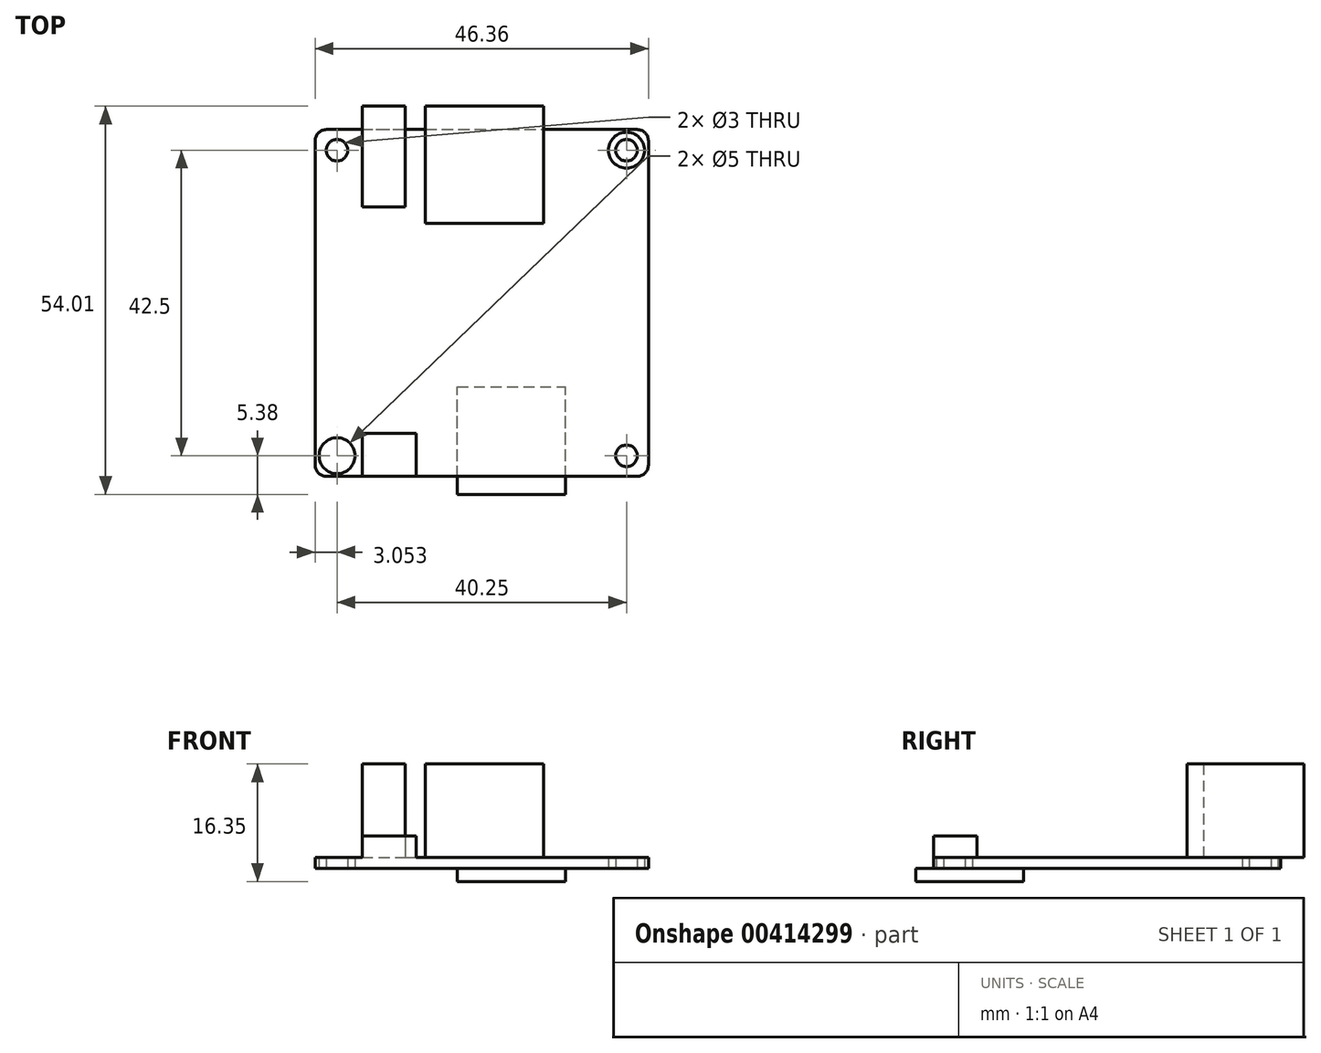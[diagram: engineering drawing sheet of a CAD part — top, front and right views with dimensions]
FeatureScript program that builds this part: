
annotation { "Feature Type Name" : "Feature", "Feature Type Description" : "" }
export const myFeature = defineFeature(function(context is Context, id is Id, definition is map)
    precondition{}
    {
        {
            var Q0;
            Q0=qCreatedBy(makeId("Top.planeOp"),FACE);
            var sketch = newSketch(context, id + "F0", { "sketchPlane" : qUnion([Q0])});
            skLineSegment(sketch, "E0.bottom", {"start": v(1.59, 0) * mm, "end": v(44.77, 0) * mm});
            skLineSegment(sketch, "E0.top", {"start": v(1.59, 48.26) * mm, "end": v(44.77, 48.26) * mm});
            skLineSegment(sketch, "E0.left", {"start": v(0, 1.59) * mm, "end": v(0, 46.67) * mm});
            skLineSegment(sketch, "E0.right", {"start": v(46.35, 1.59) * mm, "end": v(46.35, 46.67) * mm});
            skCircle(sketch, "E1", {"center": v(43.3, 2.88) * mm, "radius": 2.5 * mm});
            skLineSegment(sketch, "E2", {"start": v(23.18, 48.26) * mm, "end": v(23.18, 0) * mm, "construction": true});
            skLineSegment(sketch, "E3", {"start": v(0, 24.13) * mm, "end": v(46.35, 24.13) * mm, "construction": true});
            skCircle(sketch, "E4", {"center": v(43.3, 2.88) * mm, "radius": 1.5 * mm});
            skCircle(sketch, "E5.MirrorC", {"center": v(43.3, 45.38) * mm, "radius": 1.5 * mm});
            skCircle(sketch, "E6.MirrorC", {"center": v(43.3, 45.38) * mm, "radius": 2.5 * mm});
            skCircle(sketch, "E7.MirrorC", {"center": v(3.05, 2.88) * mm, "radius": 2.5 * mm});
            skCircle(sketch, "E8.MirrorC", {"center": v(3.05, 45.38) * mm, "radius": 2.5 * mm});
            skCircle(sketch, "E9.MirrorC", {"center": v(3.05, 45.38) * mm, "radius": 1.5 * mm});
            skCircle(sketch, "E10.MirrorC", {"center": v(3.05, 2.88) * mm, "radius": 1.5 * mm});
            skPoint(sketch, "E11.visualSharp", {"position": v(0, 48.26) * mm});
            skArc(sketch, "E11.filletArc", {"start": v(1.59, 48.26) * mm, "mid": v(0.46, 47.8) * mm, "end": v(0, 46.67) * mm});
            skPoint(sketch, "E12.visualSharp", {"position": v(46.35, 48.26) * mm});
            skArc(sketch, "E12.filletArc", {"start": v(46.35, 46.67) * mm, "mid": v(45.9, 47.8) * mm, "end": v(44.77, 48.26) * mm});
            skPoint(sketch, "E13.visualSharp", {"position": v(0, 0) * mm});
            skArc(sketch, "E13.filletArc", {"start": v(0, 1.59) * mm, "mid": v(0.46, 0.46) * mm, "end": v(1.59, 0) * mm});
            skPoint(sketch, "E14.visualSharp", {"position": v(46.35, 0) * mm});
            skArc(sketch, "E14.filletArc", {"start": v(44.77, 0) * mm, "mid": v(45.9, 0.46) * mm, "end": v(46.35, 1.59) * mm});
            skSolve(sketch);
        }
        {
            var Q0;
            Q0=makeQuery(id+"F0.imprint","IMPRINT",FACE,{"disambiguationData":[TD([[makeQuery(id+"F0.imprint","IMPRINT",EDGE,{"derivedFrom":sQuery(id+"F0.wireOp",EDGE,"E0.bottom")}),1.0]])]});
            var Q1;
            Q1=makeQuery(id+"F0.imprint","IMPRINT",FACE,{"disambiguationData":[TD([[makeQuery(id+"F0.imprint","IMPRINT",EDGE,{"derivedFrom":sQuery(id+"F0.wireOp",EDGE,"E7.MirrorC")}),-1.0]])]});
            var Q2;
            Q2=makeQuery(id+"F0.imprint","IMPRINT",FACE,{"disambiguationData":[TD([[makeQuery(id+"F0.imprint","IMPRINT",EDGE,{"derivedFrom":sQuery(id+"F0.wireOp",EDGE,"E1")}),1.0]])]});
            var Q3;
            Q3=makeQuery(id+"F0.imprint","IMPRINT",FACE,{"disambiguationData":[TD([[makeQuery(id+"F0.imprint","IMPRINT",EDGE,{"derivedFrom":sQuery(id+"F0.wireOp",EDGE,"E5.MirrorC")}),1.0]])]});
            var Q4;
            Q4=makeQuery(id+"F0.imprint","IMPRINT",FACE,{"disambiguationData":[TD([[makeQuery(id+"F0.imprint","IMPRINT",EDGE,{"derivedFrom":sQuery(id+"F0.wireOp",EDGE,"E8.MirrorC")}),1.0]])]});
            extrude(context, id + "F1", {"entities" : qUnion([Q0, Q1, Q2, Q3, Q4]), "depth" : 1.5 * mm});
        }
        {
            var Q0;
            Q0=makeQuery(id+"F1.opExtrude","CAP_FACE",FACE,{"disambiguationData":[OSD([sQuery(id+"F0.wireOp",EDGE,"E0.bottom"),sQuery(id+"F0.wireOp",EDGE,"E0.top"),sQuery(id+"F0.wireOp",EDGE,"E0.left"),sQuery(id+"F0.wireOp",EDGE,"E0.right"),sQuery(id+"F0.wireOp",EDGE,"E4"),sQuery(id+"F0.wireOp",EDGE,"E5.MirrorC"),sQuery(id+"F0.wireOp",EDGE,"E9.MirrorC"),sQuery(id+"F0.wireOp",EDGE,"E10.MirrorC"),sQuery(id+"F0.wireOp",EDGE,"E11.filletArc"),sQuery(id+"F0.wireOp",EDGE,"E12.filletArc"),sQuery(id+"F0.wireOp",EDGE,"E13.filletArc"),sQuery(id+"F0.wireOp",EDGE,"E14.filletArc")])],"isStart":false});
            var sketch = newSketch(context, id + "F2", { "sketchPlane" : qUnion([Q0])});
            skLineSegment(sketch, "E15.bottom", {"start": v(6.55, 51.51) * mm, "end": v(12.55, 51.51) * mm});
            skLineSegment(sketch, "E15.top", {"start": v(6.55, 37.51) * mm, "end": v(12.55, 37.51) * mm});
            skLineSegment(sketch, "E15.left", {"start": v(6.55, 51.51) * mm, "end": v(6.55, 37.51) * mm});
            skLineSegment(sketch, "E15.right", {"start": v(12.55, 51.51) * mm, "end": v(12.55, 37.51) * mm});
            skLineSegment(sketch, "E16.bottom", {"start": v(15.3, 51.51) * mm, "end": v(31.8, 51.51) * mm});
            skLineSegment(sketch, "E16.top", {"start": v(15.3, 35.21) * mm, "end": v(31.8, 35.21) * mm});
            skLineSegment(sketch, "E16.left", {"start": v(15.3, 51.51) * mm, "end": v(15.3, 35.21) * mm});
            skLineSegment(sketch, "E16.right", {"start": v(31.8, 51.51) * mm, "end": v(31.8, 35.21) * mm});
            skLineSegment(sketch, "E17.bottom", {"start": v(6.55, 0) * mm, "end": v(14.05, 0) * mm});
            skLineSegment(sketch, "E17.top", {"start": v(6.55, 6) * mm, "end": v(14.05, 6) * mm});
            skLineSegment(sketch, "E17.left", {"start": v(6.55, 0) * mm, "end": v(6.55, 6) * mm});
            skLineSegment(sketch, "E17.right", {"start": v(14.05, 0) * mm, "end": v(14.05, 6) * mm});
            skLineSegment(sketch, "E18.bottom", {"start": v(19.8, -2.5) * mm, "end": v(34.8, -2.5) * mm});
            skLineSegment(sketch, "E18.top", {"start": v(19.8, 12.5) * mm, "end": v(34.8, 12.5) * mm});
            skLineSegment(sketch, "E18.left", {"start": v(19.8, -2.5) * mm, "end": v(19.8, 12.5) * mm});
            skLineSegment(sketch, "E18.right", {"start": v(34.8, -2.5) * mm, "end": v(34.8, 12.5) * mm});
            skSolve(sketch);
        }
        {
            var Q0;
            Q0=makeQuery(id+"F2.imprint","IMPRINT",FACE,{"disambiguationData":[TD([[makeQuery(id+"F2.imprint","IMPRINT",EDGE,{"derivedFrom":sQuery(id+"F2.wireOp",EDGE,"E15.bottom")}),-1.0]])]});
            var Q1;
            Q1=makeQuery(id+"F2.imprint","IMPRINT",FACE,{"disambiguationData":[TD([[makeQuery(id+"F2.imprint","IMPRINT",EDGE,{"derivedFrom":sQuery(id+"F2.wireOp",EDGE,"E16.bottom")}),-1.0]])]});
            var Q2;
            {var subQ0=sQuery(id+"F2.wireOp",EDGE,"E15.top");Q2=makeQuery(id+"F2.imprint","IMPRINT",FACE,{"disambiguationData":[TD([[makeQuery(id+"F2.imprint","IMPRINT",EDGE,{"derivedFrom":subQ0}),1.0]])]});}
            var Q3;
            {var subQ0=sQuery(id+"F2.wireOp",EDGE,"E16.top");Q3=makeQuery(id+"F2.imprint","IMPRINT",FACE,{"disambiguationData":[TD([[makeQuery(id+"F2.imprint","IMPRINT",EDGE,{"derivedFrom":subQ0}),1.0]])]});}
            extrude(context, id + "F3", {"entities" : qUnion([Q0, Q1, Q2, Q3]), "operationType" : NewBodyOperationType.ADD, "depth" : 13 * mm});
        }
        {
            var Q0;
            Q0=makeQuery(id+"F2.imprint","IMPRINT",FACE,{"disambiguationData":[TD([[makeQuery(id+"F2.imprint","IMPRINT",EDGE,{"derivedFrom":sQuery(id+"F2.wireOp",EDGE,"E17.bottom")}),1.0]])]});
            extrude(context, id + "F4", {"entities" : qUnion([Q0]), "operationType" : NewBodyOperationType.ADD, "depth" : 3 * mm});
        }
        {
            var Q0;
            Q0=makeQuery(id+"F1.opExtrude","CAP_FACE",FACE,{"disambiguationData":[OSD([sQuery(id+"F0.wireOp",EDGE,"E0.bottom"),sQuery(id+"F0.wireOp",EDGE,"E0.top"),sQuery(id+"F0.wireOp",EDGE,"E0.left"),sQuery(id+"F0.wireOp",EDGE,"E0.right"),sQuery(id+"F0.wireOp",EDGE,"E4"),sQuery(id+"F0.wireOp",EDGE,"E5.MirrorC"),sQuery(id+"F0.wireOp",EDGE,"E9.MirrorC"),sQuery(id+"F0.wireOp",EDGE,"E10.MirrorC"),sQuery(id+"F0.wireOp",EDGE,"E11.filletArc"),sQuery(id+"F0.wireOp",EDGE,"E12.filletArc"),sQuery(id+"F0.wireOp",EDGE,"E13.filletArc"),sQuery(id+"F0.wireOp",EDGE,"E14.filletArc")])],"isStart":true});
            var sketch = newSketch(context, id + "F5", { "sketchPlane" : qUnion([Q0])});
            skLineSegment(sketch, "E19.0", {"start": v(19.8, -12.5) * mm, "end": v(34.8, -12.5) * mm});
            skLineSegment(sketch, "E19.1", {"start": v(19.8, 2.5) * mm, "end": v(19.8, -12.5) * mm});
            skLineSegment(sketch, "E19.2", {"start": v(19.8, 2.5) * mm, "end": v(34.8, 2.5) * mm});
            skLineSegment(sketch, "E19.3", {"start": v(34.8, 2.5) * mm, "end": v(34.8, -12.5) * mm});
            skSolve(sketch);
        }
        {
            var Q0;
            Q0 = qSketchRegion(id + "F5", true);
            extrude(context, id + "F6", {"entities" : qUnion([Q0]), "operationType" : NewBodyOperationType.ADD, "depth" : 1.85 * mm});
        }
    });
